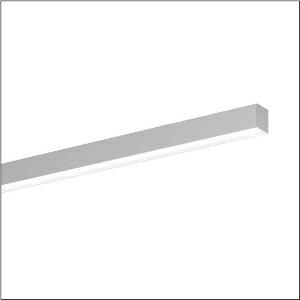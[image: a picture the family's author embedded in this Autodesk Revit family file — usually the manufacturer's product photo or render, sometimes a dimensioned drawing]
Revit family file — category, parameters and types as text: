
# Revit family: silica_r__21_51mx23dc4asb_a1ef
name_source: partatom
category: Lighting Fixtures
units: mm (PartAtom-declared; Revit-internal decimal feet)

## family parameters
Cut with Voids When Loaded = No
Host = Face
Light Source = No
Part Type = Normal
Room Calculation Point = No
Round Connector Dimension = Use Diameter
Shared = No

## types (1)
- --- (1 x LED, 8200 lm, 58.2 W, 4000K)
    Apparent Load = 58 VA
    CIE Flux Codes = 78 96 99 100 100
    Color Rendering = 80
    Color Temperature = 4000K
    Default Elevation = 1800 mm
    Description = Silica® 21, office luminaire, primary optical cover: prismatic diffuser, of PMMA, CAT 2 (L<= 3000cd/m²), light emission: direct distribution, primary light characteristic: symmetric, installation type: surface-mounted, LED, rated luminous flux: 8.200lm, luminous efficacy: 141lm/W, light colour: 840, colour temperature: 4000K, with terminal, 3+2-pole, max. 2.5mm², mains connection: 220..240V, AC, 50/60Hz, rated input power: 58.2W, luminaire housing, of aluminium, metallic grey (RAL 9006), length: 3.004mm, width: 53mm, height: 53mm, protection rating (complete): IP20, insulation class (complete): insulation class I (protective earthing), certification: CE, permissible operating ambient temperature: 0..+35°C, standard: EN 50419, packaging unit: 1 piece
    Height = 0 mm  [stored 0 ft]
    Lamp = 1 x LED
    Lamp Light Flux = 8200 lm
    Lamp Power = 58.2 W
    Lamp count = 1
    Length = 3004 mm
    Luminous efficacy = 141 lm/W
    Manufacturer = Siteco
    ModVariant = No
    Model = 51MX23DC4ASB
    Mounting Place = Ceiling
    Mounting Type = Recessed
    Number of Poles = 1
    OnlyDefault = Yes
    Power Factor = 1
    Product Name = Silica® 21
    Product group = office luminaire | ceiling recessed
    ProductGroupID = 401
    Protection Class = Protection class I
    Protection Degree = IP 20
    RLX_Detail_Level = 1
    RLX_Emergency_Light_Flux = 0 lm
    RLX_Emergency_Type = 0
    RLX_Emergency_Type_DB = No
    RlxData = <blob elided: 21097 chars, md5=c3e1ec8f>
    Socket = socket
    Standby Power = 0 W
    System Light Flux = 8200 lm
    System Power = 58 W
    Type Comments = factory setting: luminous flux: 100 % | dim-lin: 254 | 323 mA
    Type Image = l_1297768.jpg
    URL = http://relux.com
    VarID = @adj_049613
    Voltage = 0 V
    Weight = 0.00 kg
    Width = 53 mm

note: [stored X ft] marks values corroborated as IEEE doubles in the binary element streams (Revit-internal decimal feet)

## geometry (parser evidence)
native form markers: Blend x4, Sweep x9
no freeform markers — native parametric forms only
